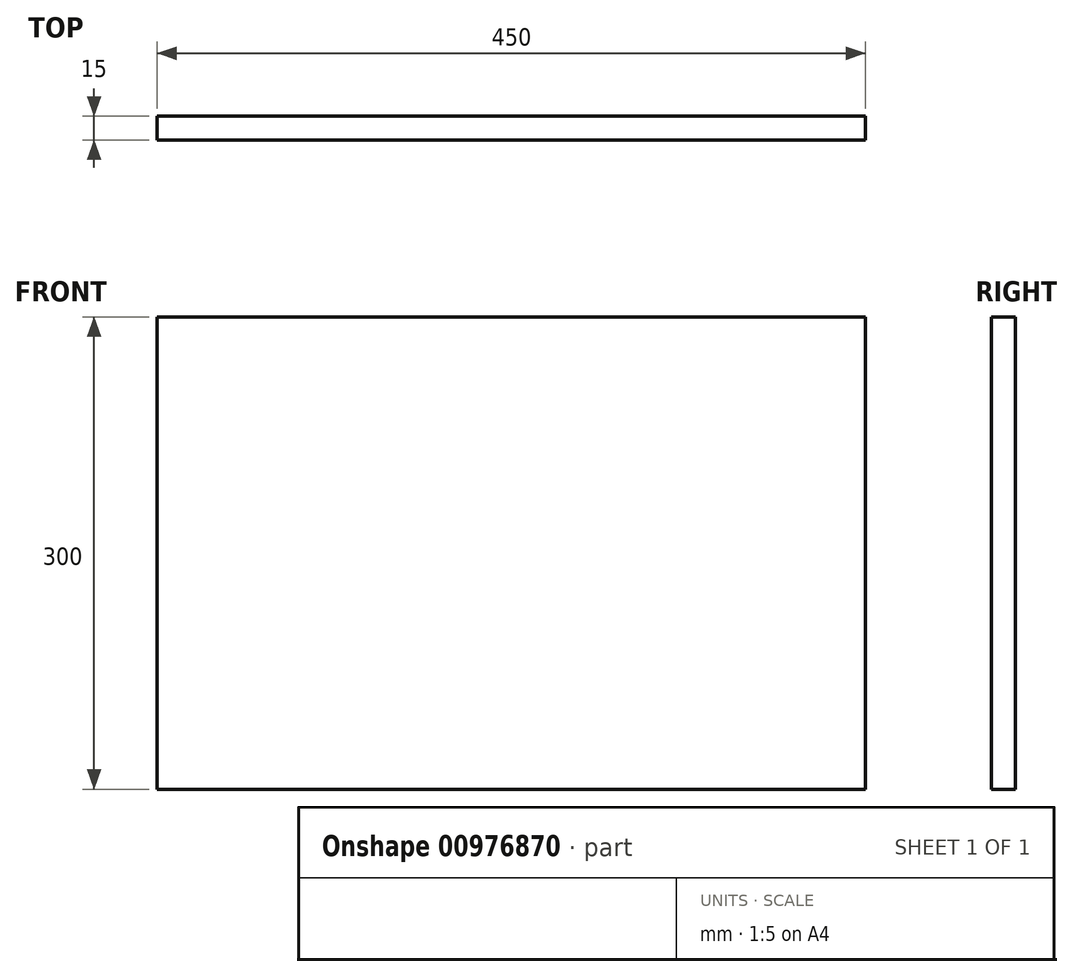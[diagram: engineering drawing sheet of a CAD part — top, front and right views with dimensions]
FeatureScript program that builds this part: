
annotation { "Feature Type Name" : "Feature", "Feature Type Description" : "" }
export const myFeature = defineFeature(function(context is Context, id is Id, definition is map)
    precondition{}
    {
        {
            var Q0;
            Q0=qCreatedBy(makeId("Front.planeOp"),FACE);
            var sketch = newSketch(context, id + "F0", { "sketchPlane" : qUnion([Q0])});
            skLineSegment(sketch, "E0.bottom", {"start": v(225, 150) * mm, "end": v(-225, 150) * mm});
            skLineSegment(sketch, "E0.top", {"start": v(225, -150) * mm, "end": v(-225, -150) * mm});
            skLineSegment(sketch, "E0.left", {"start": v(225, 150) * mm, "end": v(225, -150) * mm});
            skLineSegment(sketch, "E0.right", {"start": v(-225, 150) * mm, "end": v(-225, -150) * mm});
            skPoint(sketch, "E0.middle", {"position": v(0, 0) * mm});
            skSolve(sketch);
        }
        {
            var Q0;
            Q0=makeQuery(id+"F0.imprint","IMPRINT",FACE,{"disambiguationData":[TD([[makeQuery(id+"F0.imprint","IMPRINT",EDGE,{"derivedFrom":sQuery(id+"F0.wireOp",EDGE,"E0.bottom")}),1.0]])]});
            extrude(context, id + "F1", {"entities" : qUnion([Q0]), "depth" : 15 * mm, "offsetDistance" : 25 * mm});
        }
    });
